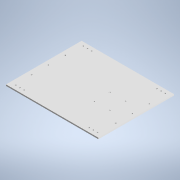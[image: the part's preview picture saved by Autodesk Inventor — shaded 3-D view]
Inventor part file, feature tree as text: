
AUTODESK INVENTOR PART (.ipt)
format: ipt  version: 2022 (Build 260153000, 153)  size: 141,824 bytes
history: native  units: mm
features: reference x22, other x11, extrude x4, sketch x4
ambient origin geometry x8: Origin, YZ Plane, XZ Plane, XY Plane, X Axis, Y Axis, Z Axis, Center Point
bodies: Body1 (feature_tree)
feature tree (41):
  other  "Твердое тело1"
  extrude  "Выдавливание1"  Depth=220.0mm
  extrude  "Выдавливание4"  Depth=180.0mm
  extrude  "Выдавливание5"  Depth=3.0mm TaperAngle=0.0deg
  extrude  "Выдавливание6"  Depth=3.0mm TaperAngle=0.0deg
  sketch  "Эскиз1"
  sketch  "Эскиз4"
  reference  "Ссылка1"
  reference  "Ссылка2"
  reference  "Ссылка3"
  reference  "Ссылка4"
  reference  "Ссылка5"
  reference  "Ссылка6"
  sketch  "Эскиз5"
  reference  "Ссылка7"
  reference  "Ссылка8"
  reference  "Ссылка9"
  reference  "Ссылка10"
  reference  "Ссылка11"
  reference  "Ссылка12"
  reference  "Ссылка13"
  reference  "Ссылка14"
  reference  "Ссылка15"
  reference  "Ссылка16"
  reference  "Ссылка17"
  reference  "Ссылка18"
  sketch  "Эскиз6"
  reference  "Ссылка19"
  reference  "Ссылка20"
  reference  "Ссылка21"
  reference  "Ссылка22"
  other  "<path> - Robot.iam"
  other  "000.000 - Robot.iam"
  other  "000.002 - bamper:2"
  other  "000.002 - bamper:1"
  other  "01_Крепление_мотора:2"
  other  "01_Крепление_мотора:4"
  other  "01_Крепление_мотора:3"
  other  "01_Крепление_мотора:1"
  other  "<path> - Robot.iam"
  other  "L298N Driver DC Motor, Stepper Motor:1"
note: 2 file-system paths scrubbed to <path> (originals preserved in map.json)
